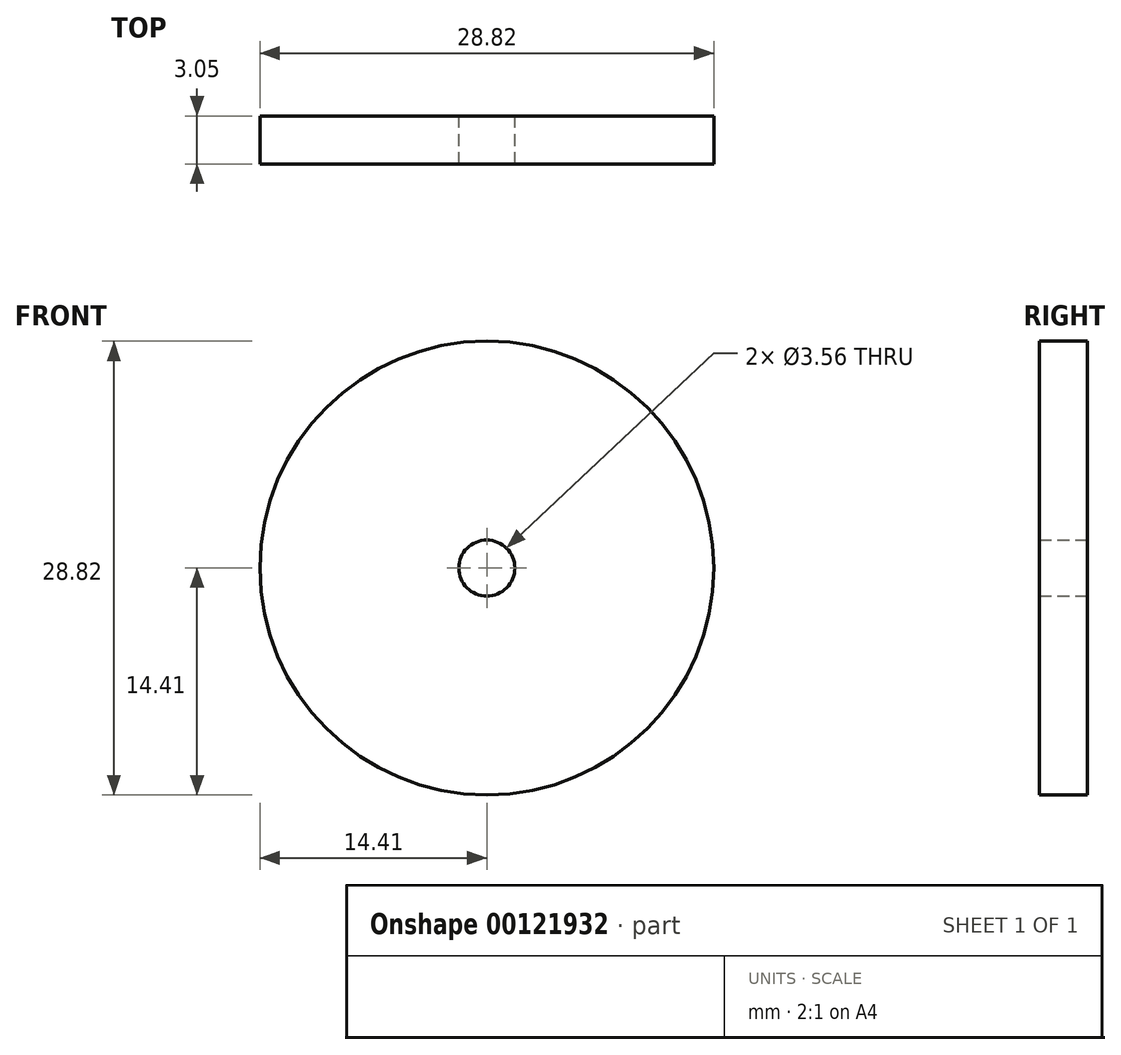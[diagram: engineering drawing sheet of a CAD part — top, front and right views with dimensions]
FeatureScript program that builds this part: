
annotation { "Feature Type Name" : "Feature", "Feature Type Description" : "" }
export const myFeature = defineFeature(function(context is Context, id is Id, definition is map)
    precondition{}
    {
        {
            var Q0;
            Q0=qCreatedBy(makeId("Front.planeOp"),FACE);
            var sketch = newSketch(context, id + "F0", { "sketchPlane" : qUnion([Q0])});
            skCircle(sketch, "E0", {"center": v(0, 0) * mm, "radius": 14.41 * mm});
            skCircle(sketch, "E1", {"center": v(0, 0) * mm, "radius": 1.78 * mm});
            skSolve(sketch);
        }
        {
            var Q0;
            Q0 = qSketchRegion(id + "F0", true);
            extrude(context, id + "F1", {"entities" : qUnion([Q0]), "depth" : 3.05 * mm});
        }
    });
